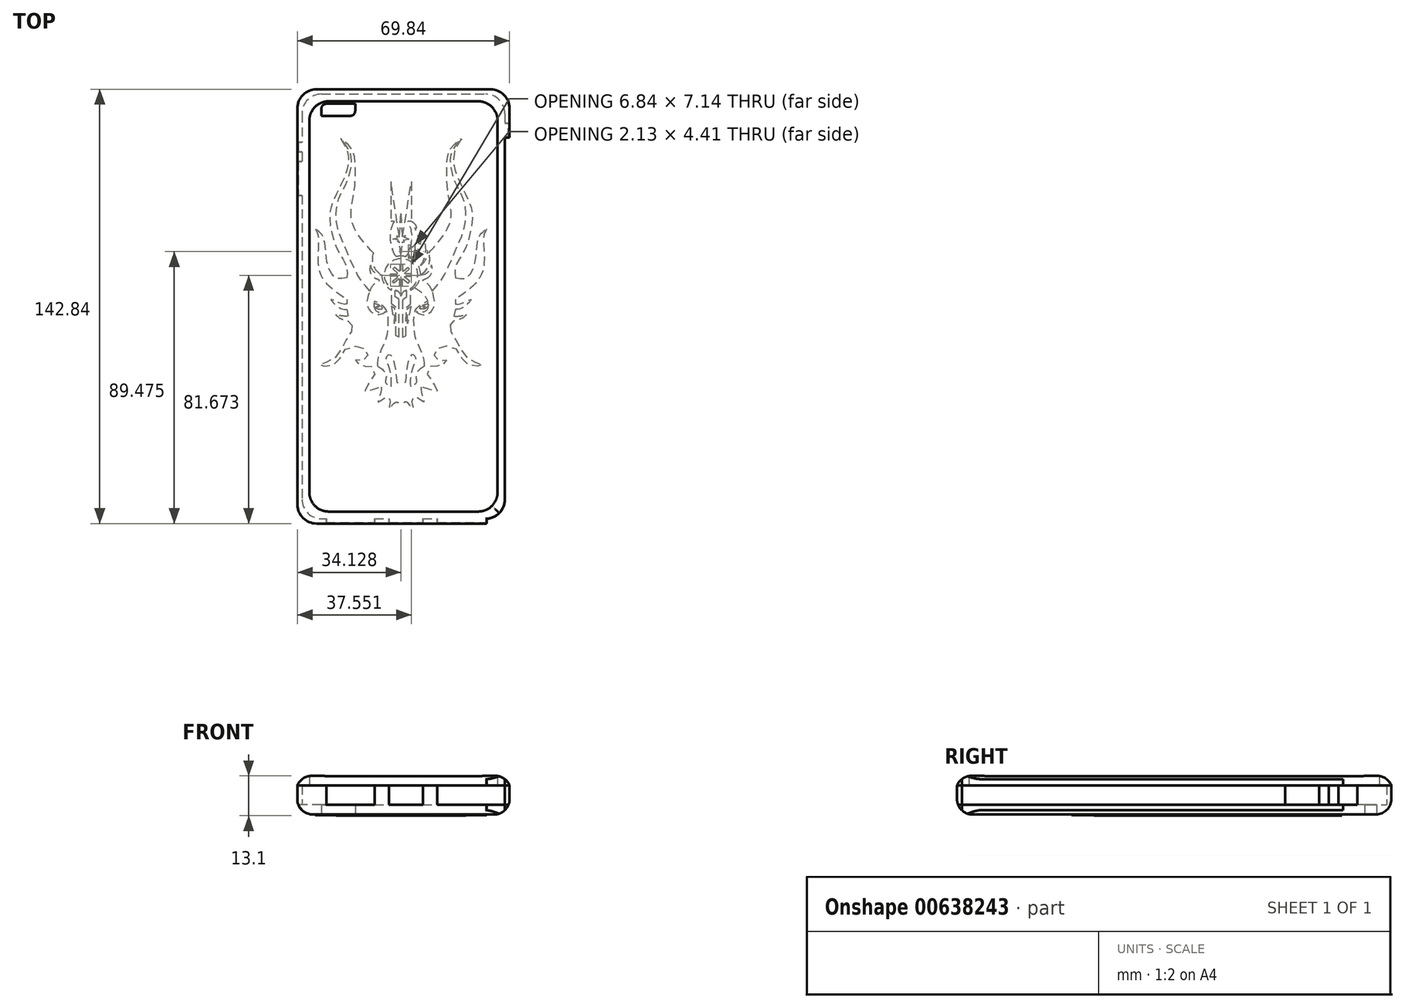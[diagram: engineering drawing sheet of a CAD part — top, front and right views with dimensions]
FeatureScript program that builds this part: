
annotation { "Feature Type Name" : "Feature", "Feature Type Description" : "" }
export const myFeature = defineFeature(function(context is Context, id is Id, definition is map)
    precondition{}
    {
        {
            var Q0;
            Q0=qCreatedBy(makeId("Top.planeOp"),FACE);
            var sketch = newSketch(context, id + "F0", { "sketchPlane" : qUnion([Q0])});
            skLineSegment(sketch, "E0.bottom", {"start": v(-25.4, 66.66) * mm, "end": v(-15.87, 66.66) * mm});
            skLineSegment(sketch, "E0.top", {"start": v(-26.98, 62.7) * mm, "end": v(-17.45, 62.7) * mm});
            skLineSegment(sketch, "E0.left", {"start": v(-26.98, 65.07) * mm, "end": v(-26.98, 62.7) * mm});
            skLineSegment(sketch, "E0.right", {"start": v(-15.87, 66.66) * mm, "end": v(-15.87, 64.28) * mm});
            skArc(sketch, "E1.filletArc", {"start": v(-25.4, 66.66) * mm, "mid": v(-26.51, 66.2) * mm, "end": v(-26.98, 65.07) * mm});
            skArc(sketch, "E2.filletArc", {"start": v(-17.45, 62.7) * mm, "mid": v(-16.33, 63.16) * mm, "end": v(-15.87, 64.28) * mm});
            skLineSegment(sketch, "E3.bottom", {"start": v(-34.92, 50.83) * mm, "end": v(-33.34, 50.83) * mm});
            skLineSegment(sketch, "E3.top", {"start": v(-34.92, 54) * mm, "end": v(-33.34, 54) * mm});
            skLineSegment(sketch, "E4.bottom", {"start": v(-34.92, 47.66) * mm, "end": v(-33.34, 47.66) * mm});
            skLineSegment(sketch, "E4.top", {"start": v(-34.92, 36.55) * mm, "end": v(-33.34, 36.55) * mm});
            skLineSegment(sketch, "E5.bottom", {"start": v(34.92, 60.29) * mm, "end": v(33.33, 60.29) * mm});
            skLineSegment(sketch, "E5.top", {"start": v(34.92, 55.52) * mm, "end": v(33.33, 55.52) * mm});
            skLineSegment(sketch, "E6.bottom", {"start": v(26.99, -69.85) * mm, "end": v(-26.99, -69.85) * mm});
            skLineSegment(sketch, "E6.top", {"start": v(26.99, 69.85) * mm, "end": v(-26.99, 69.85) * mm});
            skLineSegment(sketch, "E6.left", {"start": v(33.34, -63.5) * mm, "end": v(33.34, 63.5) * mm});
            skLineSegment(sketch, "E6.right", {"start": v(-33.34, -63.5) * mm, "end": v(-33.34, 63.5) * mm});
            skPoint(sketch, "E6.middle", {"position": v(0, 0) * mm});
            skLineSegment(sketch, "E7.bottom", {"start": v(28.57, 71.42) * mm, "end": v(-28.57, 71.42) * mm});
            skLineSegment(sketch, "E7.top", {"start": v(28.57, -71.42) * mm, "end": v(-28.57, -71.42) * mm});
            skLineSegment(sketch, "E7.left", {"start": v(34.92, 65.07) * mm, "end": v(34.92, -65.07) * mm});
            skLineSegment(sketch, "E7.right", {"start": v(-34.92, 65.07) * mm, "end": v(-34.92, -65.07) * mm});
            skLineSegment(sketch, "E8.bottom", {"start": v(24.6, -67.47) * mm, "end": v(-24.6, -67.47) * mm});
            skLineSegment(sketch, "E8.top", {"start": v(24.6, 67.47) * mm, "end": v(-24.6, 67.47) * mm});
            skLineSegment(sketch, "E8.left", {"start": v(30.96, -61.12) * mm, "end": v(30.96, 61.12) * mm});
            skLineSegment(sketch, "E8.right", {"start": v(-30.96, -61.12) * mm, "end": v(-30.96, 61.12) * mm});
            skPoint(sketch, "E9.visualSharp", {"position": v(-30.96, -67.47) * mm});
            skPoint(sketch, "E10.visualSharp", {"position": v(30.96, -67.47) * mm});
            skPoint(sketch, "E11.visualSharp", {"position": v(33.34, -69.85) * mm});
            skPoint(sketch, "E12.visualSharp", {"position": v(-33.34, -69.85) * mm});
            skPoint(sketch, "E13.visualSharp", {"position": v(-34.92, -71.42) * mm});
            skPoint(sketch, "E14.visualSharp", {"position": v(34.92, -71.42) * mm});
            skPoint(sketch, "E15.visualSharp", {"position": v(-34.92, 71.42) * mm});
            skPoint(sketch, "E16.visualSharp", {"position": v(-33.34, 69.85) * mm});
            skPoint(sketch, "E17.visualSharp", {"position": v(-30.96, 67.47) * mm});
            skPoint(sketch, "E18.visualSharp", {"position": v(30.96, 67.47) * mm});
            skPoint(sketch, "E19.visualSharp", {"position": v(33.34, 69.85) * mm});
            skPoint(sketch, "E20.visualSharp", {"position": v(34.92, 71.42) * mm});
            skLineSegment(sketch, "E21", {"start": v(-28.57, -71.42) * mm, "end": v(28.57, -71.42) * mm});
            skLineSegment(sketch, "E22.bottom", {"start": v(-25.4, -71.42) * mm, "end": v(-9.52, -71.42) * mm});
            skLineSegment(sketch, "E22.top", {"start": v(-25.4, -69.85) * mm, "end": v(-9.52, -69.85) * mm});
            skLineSegment(sketch, "E22.left", {"start": v(-25.4, -71.42) * mm, "end": v(-25.4, -69.85) * mm});
            skLineSegment(sketch, "E22.right", {"start": v(-9.52, -71.42) * mm, "end": v(-9.52, -69.85) * mm});
            skLineSegment(sketch, "E23.bottom", {"start": v(-4.76, -71.42) * mm, "end": v(6.36, -71.42) * mm});
            skLineSegment(sketch, "E23.top", {"start": v(-4.76, -69.85) * mm, "end": v(6.36, -69.85) * mm});
            skLineSegment(sketch, "E23.left", {"start": v(-4.76, -71.42) * mm, "end": v(-4.76, -69.85) * mm});
            skLineSegment(sketch, "E23.right", {"start": v(6.36, -71.42) * mm, "end": v(6.36, -69.85) * mm});
            skLineSegment(sketch, "E24", {"start": v(-28.57, -71.42) * mm, "end": v(12.42, -71.42) * mm});
            skLineSegment(sketch, "E25", {"start": v(-28.57, -71.42) * mm, "end": v(11.12, -71.42) * mm});
            skLineSegment(sketch, "E26.bottom", {"start": v(11.12, -71.42) * mm, "end": v(27.4, -71.42) * mm});
            skLineSegment(sketch, "E26.top", {"start": v(11.12, -69.85) * mm, "end": v(27.4, -69.85) * mm});
            skLineSegment(sketch, "E26.left", {"start": v(11.12, -71.42) * mm, "end": v(11.12, -69.85) * mm});
            skLineSegment(sketch, "E26.right", {"start": v(27.4, -71.42) * mm, "end": v(27.4, -69.85) * mm});
            skLineSegment(sketch, "E27", {"start": v(-24.6, -67.47) * mm, "end": v(24.6, -67.47) * mm});
            skLineSegment(sketch, "E28", {"start": v(-33.34, 63.5) * mm, "end": v(-33.34, -63.5) * mm});
            skLineSegment(sketch, "E29", {"start": v(-26.99, -69.85) * mm, "end": v(27.4, -69.85) * mm});
            skLineSegment(sketch, "E30", {"start": v(33.34, -69.85) * mm, "end": v(33.34, -69.27) * mm});
            skLineSegment(sketch, "E31", {"start": v(-28.57, 71.42) * mm, "end": v(28.57, 71.42) * mm});
            skLineSegment(sketch, "E32", {"start": v(34.92, -65.07) * mm, "end": v(34.92, 65.07) * mm});
            skLineSegment(sketch, "E33", {"start": v(-34.92, -65.07) * mm, "end": v(-34.92, 65.07) * mm});
            skArc(sketch, "E34.filletArc", {"start": v(-30.96, -61.12) * mm, "mid": v(-29.1, -65.6) * mm, "end": v(-24.6, -67.47) * mm});
            skArc(sketch, "E35.filletArc", {"start": v(-33.34, -63.5) * mm, "mid": v(-31.48, -68) * mm, "end": v(-26.99, -69.85) * mm});
            skArc(sketch, "E36.filletArc", {"start": v(-34.92, -65.07) * mm, "mid": v(-33.06, -69.56) * mm, "end": v(-28.57, -71.42) * mm});
            skArc(sketch, "E37.filletArc", {"start": v(28.57, -71.42) * mm, "mid": v(33.06, -69.56) * mm, "end": v(34.92, -65.07) * mm});
            skArc(sketch, "E38.filletArc", {"start": v(26.99, -69.85) * mm, "mid": v(31.48, -68) * mm, "end": v(33.34, -63.5) * mm});
            skArc(sketch, "E39.filletArc", {"start": v(24.6, -67.47) * mm, "mid": v(29.1, -65.6) * mm, "end": v(30.96, -61.12) * mm});
            skArc(sketch, "E40.filletArc", {"start": v(-24.6, 67.47) * mm, "mid": v(-29.1, 65.6) * mm, "end": v(-30.96, 61.12) * mm});
            skArc(sketch, "E41.filletArc", {"start": v(-26.99, 69.85) * mm, "mid": v(-31.48, 68) * mm, "end": v(-33.34, 63.5) * mm});
            skArc(sketch, "E42.filletArc", {"start": v(-28.57, 71.42) * mm, "mid": v(-33.06, 69.56) * mm, "end": v(-34.92, 65.07) * mm});
            skArc(sketch, "E43.filletArc", {"start": v(34.92, 65.07) * mm, "mid": v(33.06, 69.56) * mm, "end": v(28.57, 71.42) * mm});
            skArc(sketch, "E44.filletArc", {"start": v(33.34, 63.5) * mm, "mid": v(31.48, 68) * mm, "end": v(26.99, 69.85) * mm});
            skArc(sketch, "E45.filletArc", {"start": v(30.96, 61.12) * mm, "mid": v(29.1, 65.6) * mm, "end": v(24.6, 67.47) * mm});
            skLineSegment(sketch, "E46.trimOffspring", {"start": v(32.75, -69.85) * mm, "end": v(33.34, -69.85) * mm});
            skSolve(sketch);
        }
        {
            var Q0;
            Q0=makeQuery(id+"F0.imprint","IMPRINT",FACE,{"disambiguationData":[TD([[makeQuery(id+"F0.imprint","IMPRINT",EDGE,{"derivedFrom":sQuery(id+"F0.wireOp",EDGE,"E0.bottom")}),1.0]])]});
            var Q1;
            Q1=makeQuery(id+"F0.imprint","IMPRINT",FACE,{"disambiguationData":[TD([[makeQuery(id+"F0.imprint","IMPRINT",EDGE,{"derivedFrom":sQuery(id+"F0.wireOp",EDGE,"E8.right")}),1.0]])]});
            var Q2;
            {var subQ0=sQuery(id+"F0.wireOp",EDGE,"E28");var subQ1=sQuery(id+"F0.wireOp",EDGE,"E3.bottom");var subQ2=makeQuery(id+"F0.imprint","INTERSECT",VERTEX,{"derivedFrom":[subQ1,subQ0]});Q2=makeQuery(id+"F0.imprint","IMPRINT",FACE,{"disambiguationData":[TD([[makeQuery(id+"F0.imprint","IMPRINT",EDGE,{"disambiguationData":[TD([[subQ2,1.0]])],"derivedFrom":subQ1}),1.0]])]});}
            var Q3;
            {var subQ0=sQuery(id+"F0.wireOp",EDGE,"E28");var subQ1=sQuery(id+"F0.wireOp",EDGE,"E3.bottom");var subQ2=makeQuery(id+"F0.imprint","INTERSECT",VERTEX,{"derivedFrom":[subQ1,subQ0]});Q3=makeQuery(id+"F0.imprint","IMPRINT",FACE,{"disambiguationData":[TD([[makeQuery(id+"F0.imprint","IMPRINT",EDGE,{"disambiguationData":[TD([[subQ2,1.0]])],"derivedFrom":subQ1}),-1.0]])]});}
            var Q4;
            {var subQ0=sQuery(id+"F0.wireOp",EDGE,"E28");var subQ1=sQuery(id+"F0.wireOp",EDGE,"E4.bottom");var subQ2=makeQuery(id+"F0.imprint","INTERSECT",VERTEX,{"derivedFrom":[subQ1,subQ0]});Q4=makeQuery(id+"F0.imprint","IMPRINT",FACE,{"disambiguationData":[TD([[makeQuery(id+"F0.imprint","IMPRINT",EDGE,{"disambiguationData":[TD([[subQ2,1.0]])],"derivedFrom":subQ1}),-1.0]])]});}
            var Q5;
            Q5=makeQuery(id+"F0.imprint","IMPRINT",FACE,{"disambiguationData":[TD([[makeQuery(id+"F0.imprint","IMPRINT",EDGE,{"derivedFrom":sQuery(id+"F0.wireOp",EDGE,"E6.top")}),-1.0]])]});
            var Q6;
            {var subQ5=sQuery(id+"F0.wireOp",EDGE,"E22.left");Q6=makeQuery(id+"F0.imprint","IMPRINT",FACE,{"disambiguationData":[TD([[makeQuery(id+"F0.imprint","IMPRINT",EDGE,{"derivedFrom":subQ5}),1.0]])]});}
            var Q7;
            {var subQ0=sQuery(id+"F0.wireOp",EDGE,"E32");var subQ1=sQuery(id+"F0.wireOp",EDGE,"E5.bottom");var subQ2=makeQuery(id+"F0.imprint","INTERSECT",VERTEX,{"derivedFrom":[subQ1,subQ0]});Q7=makeQuery(id+"F0.imprint","IMPRINT",FACE,{"disambiguationData":[TD([[makeQuery(id+"F0.imprint","IMPRINT",EDGE,{"disambiguationData":[TD([[subQ2,-1.0]])],"derivedFrom":subQ1}),1.0]])]});}
            var Q8;
            {var subQ3=sQuery(id+"F0.wireOp",EDGE,"E21");Q8=makeQuery(id+"F0.imprint","IMPRINT",FACE,{"disambiguationData":[TD([[makeQuery(id+"F0.imprint","IMPRINT",EDGE,{"derivedFrom":subQ3}),1.0]])]});}
            var Q9;
            {var subQ2=sQuery(id+"F0.wireOp",EDGE,"E26.left");Q9=makeQuery(id+"F0.imprint","IMPRINT",FACE,{"disambiguationData":[TD([[makeQuery(id+"F0.imprint","IMPRINT",EDGE,{"derivedFrom":subQ2}),-1.0]])]});}
            var Q10;
            {var subQ0=sQuery(id+"F0.wireOp",EDGE,"E23.right");Q10=makeQuery(id+"F0.imprint","IMPRINT",FACE,{"disambiguationData":[TD([[makeQuery(id+"F0.imprint","IMPRINT",EDGE,{"derivedFrom":subQ0}),-1.0]])]});}
            var Q11;
            {var subQ0=sQuery(id+"F0.wireOp",EDGE,"E23.left");Q11=makeQuery(id+"F0.imprint","IMPRINT",FACE,{"disambiguationData":[TD([[makeQuery(id+"F0.imprint","IMPRINT",EDGE,{"derivedFrom":subQ0}),-1.0]])]});}
            var Q12;
            {var subQ0=sQuery(id+"F0.wireOp",EDGE,"E22.right");Q12=makeQuery(id+"F0.imprint","IMPRINT",FACE,{"disambiguationData":[TD([[makeQuery(id+"F0.imprint","IMPRINT",EDGE,{"derivedFrom":subQ0}),-1.0]])]});}
            var Q13;
            {var subQ0=sQuery(id+"F0.wireOp",EDGE,"E22.left");Q13=makeQuery(id+"F0.imprint","IMPRINT",FACE,{"disambiguationData":[TD([[makeQuery(id+"F0.imprint","IMPRINT",EDGE,{"derivedFrom":subQ0}),-1.0]])]});}
            extrude(context, id + "F1", {"entities" : qUnion([Q0, Q1, Q2, Q3, Q4, Q5, Q6, Q7, Q8, Q9, Q10, Q11, Q12, Q13]), "depth" : 3.17 * mm, "offsetDistance" : 25.4 * mm});
        }
        {
            var Q0;
            {var subQ5=sQuery(id+"F0.wireOp",EDGE,"E22.left");Q0=makeQuery(id+"F0.imprint","IMPRINT",FACE,{"disambiguationData":[TD([[makeQuery(id+"F0.imprint","IMPRINT",EDGE,{"derivedFrom":subQ5}),1.0]])]});}
            var Q1;
            {var subQ0=sQuery(id+"F0.wireOp",EDGE,"E28");var subQ1=sQuery(id+"F0.wireOp",EDGE,"E3.bottom");var subQ2=makeQuery(id+"F0.imprint","INTERSECT",VERTEX,{"derivedFrom":[subQ1,subQ0]});Q1=makeQuery(id+"F0.imprint","IMPRINT",FACE,{"disambiguationData":[TD([[makeQuery(id+"F0.imprint","IMPRINT",EDGE,{"disambiguationData":[TD([[subQ2,1.0]])],"derivedFrom":subQ1}),-1.0]])]});}
            var Q2;
            Q2=makeQuery(id+"F0.imprint","IMPRINT",FACE,{"disambiguationData":[TD([[makeQuery(id+"F0.imprint","IMPRINT",EDGE,{"derivedFrom":sQuery(id+"F0.wireOp",EDGE,"E6.top")}),-1.0]])]});
            var Q3;
            {var subQ3=sQuery(id+"F0.wireOp",EDGE,"E21");Q3=makeQuery(id+"F0.imprint","IMPRINT",FACE,{"disambiguationData":[TD([[makeQuery(id+"F0.imprint","IMPRINT",EDGE,{"derivedFrom":subQ3}),1.0]])]});}
            var Q4;
            {var subQ0=sQuery(id+"F0.wireOp",EDGE,"E22.right");Q4=makeQuery(id+"F0.imprint","IMPRINT",FACE,{"disambiguationData":[TD([[makeQuery(id+"F0.imprint","IMPRINT",EDGE,{"derivedFrom":subQ0}),-1.0]])]});}
            var Q5;
            {var subQ0=sQuery(id+"F0.wireOp",EDGE,"E23.right");Q5=makeQuery(id+"F0.imprint","IMPRINT",FACE,{"disambiguationData":[TD([[makeQuery(id+"F0.imprint","IMPRINT",EDGE,{"derivedFrom":subQ0}),-1.0]])]});}
            extrude(context, id + "F2", {"entities" : qUnion([Q0, Q1, Q2, Q3, Q4, Q5]), "operationType" : NewBodyOperationType.ADD, "depth" : 9.52 * mm, "offsetDistance" : 25.4 * mm});
        }
        {
            var Q0;
            Q0=makeQuery(id+"F0.imprint","IMPRINT",FACE,{"disambiguationData":[TD([[makeQuery(id+"F0.imprint","IMPRINT",EDGE,{"derivedFrom":sQuery(id+"F0.wireOp",EDGE,"E8.right")}),1.0]])]});
            var Q1;
            {var subQ0=sQuery(id+"F0.wireOp",EDGE,"E28");var subQ1=sQuery(id+"F0.wireOp",EDGE,"E4.bottom");var subQ2=makeQuery(id+"F0.imprint","INTERSECT",VERTEX,{"derivedFrom":[subQ1,subQ0]});Q1=makeQuery(id+"F0.imprint","IMPRINT",FACE,{"disambiguationData":[TD([[makeQuery(id+"F0.imprint","IMPRINT",EDGE,{"disambiguationData":[TD([[subQ2,1.0]])],"derivedFrom":subQ1}),-1.0]])]});}
            var Q2;
            {var subQ0=sQuery(id+"F0.wireOp",EDGE,"E28");var subQ1=sQuery(id+"F0.wireOp",EDGE,"E3.bottom");var subQ2=makeQuery(id+"F0.imprint","INTERSECT",VERTEX,{"derivedFrom":[subQ1,subQ0]});Q2=makeQuery(id+"F0.imprint","IMPRINT",FACE,{"disambiguationData":[TD([[makeQuery(id+"F0.imprint","IMPRINT",EDGE,{"disambiguationData":[TD([[subQ2,1.0]])],"derivedFrom":subQ1}),-1.0]])]});}
            var Q3;
            {var subQ0=sQuery(id+"F0.wireOp",EDGE,"E28");var subQ1=sQuery(id+"F0.wireOp",EDGE,"E3.bottom");var subQ2=makeQuery(id+"F0.imprint","INTERSECT",VERTEX,{"derivedFrom":[subQ1,subQ0]});Q3=makeQuery(id+"F0.imprint","IMPRINT",FACE,{"disambiguationData":[TD([[makeQuery(id+"F0.imprint","IMPRINT",EDGE,{"disambiguationData":[TD([[subQ2,1.0]])],"derivedFrom":subQ1}),1.0]])]});}
            var Q4;
            Q4=makeQuery(id+"F0.imprint","IMPRINT",FACE,{"disambiguationData":[TD([[makeQuery(id+"F0.imprint","IMPRINT",EDGE,{"derivedFrom":sQuery(id+"F0.wireOp",EDGE,"E6.top")}),-1.0]])]});
            var Q5;
            {var subQ5=sQuery(id+"F0.wireOp",EDGE,"E22.left");Q5=makeQuery(id+"F0.imprint","IMPRINT",FACE,{"disambiguationData":[TD([[makeQuery(id+"F0.imprint","IMPRINT",EDGE,{"derivedFrom":subQ5}),1.0]])]});}
            var Q6;
            {var subQ0=sQuery(id+"F0.wireOp",EDGE,"E32");var subQ1=sQuery(id+"F0.wireOp",EDGE,"E5.bottom");var subQ2=makeQuery(id+"F0.imprint","INTERSECT",VERTEX,{"derivedFrom":[subQ1,subQ0]});Q6=makeQuery(id+"F0.imprint","IMPRINT",FACE,{"disambiguationData":[TD([[makeQuery(id+"F0.imprint","IMPRINT",EDGE,{"disambiguationData":[TD([[subQ2,-1.0]])],"derivedFrom":subQ1}),1.0]])]});}
            var Q7;
            {var subQ3=sQuery(id+"F0.wireOp",EDGE,"E21");Q7=makeQuery(id+"F0.imprint","IMPRINT",FACE,{"disambiguationData":[TD([[makeQuery(id+"F0.imprint","IMPRINT",EDGE,{"derivedFrom":subQ3}),1.0]])]});}
            var Q8;
            {var subQ0=sQuery(id+"F0.wireOp",EDGE,"E22.left");Q8=makeQuery(id+"F0.imprint","IMPRINT",FACE,{"disambiguationData":[TD([[makeQuery(id+"F0.imprint","IMPRINT",EDGE,{"derivedFrom":subQ0}),-1.0]])]});}
            var Q9;
            {var subQ0=sQuery(id+"F0.wireOp",EDGE,"E22.right");Q9=makeQuery(id+"F0.imprint","IMPRINT",FACE,{"disambiguationData":[TD([[makeQuery(id+"F0.imprint","IMPRINT",EDGE,{"derivedFrom":subQ0}),-1.0]])]});}
            var Q10;
            {var subQ0=sQuery(id+"F0.wireOp",EDGE,"E23.left");Q10=makeQuery(id+"F0.imprint","IMPRINT",FACE,{"disambiguationData":[TD([[makeQuery(id+"F0.imprint","IMPRINT",EDGE,{"derivedFrom":subQ0}),-1.0]])]});}
            var Q11;
            {var subQ0=sQuery(id+"F0.wireOp",EDGE,"E23.right");Q11=makeQuery(id+"F0.imprint","IMPRINT",FACE,{"disambiguationData":[TD([[makeQuery(id+"F0.imprint","IMPRINT",EDGE,{"derivedFrom":subQ0}),-1.0]])]});}
            var Q12;
            {var subQ2=sQuery(id+"F0.wireOp",EDGE,"E26.left");Q12=makeQuery(id+"F0.imprint","IMPRINT",FACE,{"disambiguationData":[TD([[makeQuery(id+"F0.imprint","IMPRINT",EDGE,{"derivedFrom":subQ2}),-1.0]])]});}
            extrude(context, id + "F3", {"entities" : qUnion([Q0, Q1, Q2, Q3, Q4, Q5, Q6, Q7, Q8, Q9, Q10, Q11, Q12]), "depth" : 12.7 * mm, "offsetDistance" : 25.4 * mm, "hasSecondDirection" : true, "secondDirectionOppositeDirection" : false, "secondDirectionDepth" : 9.52 * mm});
        }
        {
            var Q0;
            Q0=makeQuery(id+"F3.opExtrude","CAP_EDGE",EDGE,{"disambiguationData":[OSD([sQuery(id+"F0.wireOp",EDGE,"E32")])],"isStart":false});
            var Q1;
            Q1=makeQuery(id+"F3.opExtrude","CAP_EDGE",EDGE,{"disambiguationData":[OSD([sQuery(id+"F0.wireOp",EDGE,"E37.filletArc")])],"isStart":false});
            var Q2;
            Q2=makeQuery(id+"F3.opExtrude","CAP_EDGE",EDGE,{"disambiguationData":[OSD([sQuery(id+"F0.wireOp",EDGE,"E21"),sQuery(id+"F0.wireOp",EDGE,"E25"),sQuery(id+"F0.wireOp",EDGE,"E26.bottom")])],"isStart":false});
            var Q3;
            Q3=makeQuery(id+"F3.opExtrude","CAP_EDGE",EDGE,{"disambiguationData":[OSD([sQuery(id+"F0.wireOp",EDGE,"E36.filletArc")])],"isStart":false});
            var Q4;
            Q4=makeQuery(id+"F3.opExtrude","CAP_EDGE",EDGE,{"disambiguationData":[OSD([sQuery(id+"F0.wireOp",EDGE,"E33")])],"isStart":false});
            var Q5;
            Q5=makeQuery(id+"F3.opExtrude","CAP_EDGE",EDGE,{"disambiguationData":[OSD([sQuery(id+"F0.wireOp",EDGE,"E42.filletArc")])],"isStart":false});
            var Q6;
            Q6=makeQuery(id+"F3.opExtrude","CAP_EDGE",EDGE,{"disambiguationData":[OSD([sQuery(id+"F0.wireOp",EDGE,"E31")])],"isStart":false});
            var Q7;
            Q7=makeQuery(id+"F3.opExtrude","CAP_EDGE",EDGE,{"disambiguationData":[OSD([sQuery(id+"F0.wireOp",EDGE,"E43.filletArc")])],"isStart":false});
            fillet(context, id + "F4", {"entities" : qUnion([Q0, Q1, Q2, Q3, Q4, Q5, Q6, Q7]), "radius" : 5.08 * mm, "tangentPropagation" : true, "allowEdgeOverflow" : false});
        }
        {
            var Q0;
            Q0=makeQuery(id+"F1.opExtrude","CAP_EDGE",EDGE,{"disambiguationData":[OSD([sQuery(id+"F0.wireOp",EDGE,"E33")])],"isStart":true});
            var Q1;
            Q1=makeQuery(id+"F1.opExtrude","CAP_EDGE",EDGE,{"disambiguationData":[OSD([sQuery(id+"F0.wireOp",EDGE,"E42.filletArc")])],"isStart":true});
            var Q2;
            Q2=makeQuery(id+"F1.opExtrude","CAP_EDGE",EDGE,{"disambiguationData":[OSD([sQuery(id+"F0.wireOp",EDGE,"E31")])],"isStart":true});
            var Q3;
            Q3=makeQuery(id+"F1.opExtrude","CAP_EDGE",EDGE,{"disambiguationData":[OSD([sQuery(id+"F0.wireOp",EDGE,"E43.filletArc")])],"isStart":true});
            var Q4;
            Q4=makeQuery(id+"F1.opExtrude","CAP_EDGE",EDGE,{"disambiguationData":[OSD([sQuery(id+"F0.wireOp",EDGE,"E32")])],"isStart":true});
            var Q5;
            Q5=makeQuery(id+"F1.opExtrude","CAP_EDGE",EDGE,{"disambiguationData":[OSD([sQuery(id+"F0.wireOp",EDGE,"E36.filletArc")])],"isStart":true});
            var Q6;
            Q6=makeQuery(id+"F1.opExtrude","CAP_EDGE",EDGE,{"disambiguationData":[OSD([sQuery(id+"F0.wireOp",EDGE,"E21"),sQuery(id+"F0.wireOp",EDGE,"E25"),sQuery(id+"F0.wireOp",EDGE,"E26.bottom")])],"isStart":true});
            var Q7;
            Q7=makeQuery(id+"F1.opExtrude","CAP_EDGE",EDGE,{"disambiguationData":[OSD([sQuery(id+"F0.wireOp",EDGE,"E37.filletArc")])],"isStart":true});
            fillet(context, id + "F5", {"entities" : qUnion([Q0, Q1, Q2, Q3, Q4, Q5, Q6, Q7]), "radius" : 5.08 * mm, "tangentPropagation" : true, "allowEdgeOverflow" : false});
        }
        {
            var Q0;
            Q0=qCreatedBy(makeId("Top.planeOp"),FACE);
            var sketch = newSketch(context, id + "F6", { "sketchPlane" : qUnion([Q0])});
            skLineSegment(sketch, "E47", {"start": v(-0.16, -10.06) * mm, "end": v(0.84, -9.56) * mm});
            skLineSegment(sketch, "E48", {"start": v(0.84, -9.56) * mm, "end": v(0.93, -0.32) * mm});
            skLineSegment(sketch, "E49", {"start": v(0.93, -0.32) * mm, "end": v(2.34, 0.78) * mm});
            skLineSegment(sketch, "E50", {"start": v(-0.16, -10.06) * mm, "end": v(-0.16, 2.37) * mm});
            skLineSegment(sketch, "E51", {"start": v(-0.16, 2.37) * mm, "end": v(1.12, 3.23) * mm});
            skLineSegment(sketch, "E52", {"start": v(1.12, 3.23) * mm, "end": v(1.12, 5.28) * mm});
            skArc(sketch, "E53", {"start": v(-0.8, 5) * mm, "mid": v(4.73, 10.33) * mm, "end": v(-0.8, 15.67) * mm});
            skLineSegment(sketch, "E54", {"start": v(2.34, 0.78) * mm, "end": v(2.3, 5.84) * mm});
            skLineSegment(sketch, "E55", {"start": v(2, 18.88) * mm, "end": v(3.7, 20.26) * mm});
            skLineSegment(sketch, "E56", {"start": v(3.7, 20.26) * mm, "end": v(3.7, 17.07) * mm});
            skLineSegment(sketch, "E57", {"start": v(3.7, 17.07) * mm, "end": v(2.47, 15.85) * mm});
            skLineSegment(sketch, "E58", {"start": v(2.47, 15.85) * mm, "end": v(1.57, 17.44) * mm});
            skArc(sketch, "E59", {"start": v(2, 18.88) * mm, "mid": v(2.8, 23.51) * mm, "end": v(1.46, 28.02) * mm});
            skArc(sketch, "E60", {"start": v(0.61, 16.38) * mm, "mid": v(1.15, 16.85) * mm, "end": v(1.57, 17.44) * mm});
            skArc(sketch, "E61", {"start": v(4.4, 25.8) * mm, "mid": v(3.37, 27.5) * mm, "end": v(1.46, 28.02) * mm});
            skArc(sketch, "E62", {"start": v(3.87, 16.13) * mm, "mid": v(5.16, 21) * mm, "end": v(3.7, 25.8) * mm});
            skArc(sketch, "E63", {"start": v(3.87, 16.13) * mm, "mid": v(5.61, 20.27) * mm, "end": v(5.62, 24.76) * mm});
            skArc(sketch, "E64", {"start": v(7.08, 22.96) * mm, "mid": v(6.62, 24.08) * mm, "end": v(5.62, 24.76) * mm});
            skArc(sketch, "E65", {"start": v(5.62, 13.44) * mm, "mid": v(7.36, 18.1) * mm, "end": v(6.23, 22.96) * mm});
            skArc(sketch, "E66", {"start": v(5.62, 13.44) * mm, "mid": v(7.45, 15.64) * mm, "end": v(7.93, 18.47) * mm});
            skArc(sketch, "E67", {"start": v(5.62, 10.4) * mm, "mid": v(8.43, 13.96) * mm, "end": v(7.93, 18.47) * mm});
            skArc(sketch, "E68", {"start": v(5.62, 10.4) * mm, "mid": v(8.03, 11.29) * mm, "end": v(9.21, 13.57) * mm});
            skArc(sketch, "E69", {"start": v(7.08, 9) * mm, "mid": v(9.17, 10.81) * mm, "end": v(9.21, 13.57) * mm});
            skArc(sketch, "E70", {"start": v(3.6, 6.23) * mm, "mid": v(5.38, 12.27) * mm, "end": v(0.61, 16.38) * mm});
            skLineSegment(sketch, "E71", {"start": v(1.32, -0.78) * mm, "end": v(2.45, 0.08) * mm});
            skLineSegment(sketch, "E72", {"start": v(2.45, 0.08) * mm, "end": v(1.34, -5.67) * mm});
            skLineSegment(sketch, "E73", {"start": v(1.34, -5.67) * mm, "end": v(1.32, -0.78) * mm});
            skFitSpline(sketch, "E74", {"points": [v(3.6, 6.23) * mm, v(6.58, 4) * mm, v(7.91, 1.72) * mm, v(8, -0.37) * mm, v(7, -1.73) * mm, v(5.03, -1.92) * mm, v(4.12, -1.7) * mm], "startDerivative": vector(14.8, -9.52) * mm, "endDerivative": vector(-7.08, 2.25) * mm});
            skFitSpline(sketch, "E75", {"points": [v(4.12, -1.7) * mm, v(5.5, -2.52) * mm, v(8.07, -2.49) * mm, v(10.12, 0.14) * mm, v(10.06, 2.7) * mm, v(8.16, 7.25) * mm, v(6.36, 8.55) * mm, v(7.08, 9) * mm], "startDerivative": vector(10.53, -7.87) * mm, "endDerivative": vector(13.03, 5.28) * mm});
            skLineSegment(sketch, "E76", {"start": v(-0.8, 16.9) * mm, "end": v(-0.27, 20.83) * mm});
            skLineSegment(sketch, "E77", {"start": v(-0.27, 20.83) * mm, "end": v(-0.27, 21.3) * mm});
            skLineSegment(sketch, "E78", {"start": v(-0.27, 21.3) * mm, "end": v(0.32, 21.3) * mm});
            skLineSegment(sketch, "E79", {"start": v(0.32, 21.3) * mm, "end": v(0.1, 21.91) * mm});
            skLineSegment(sketch, "E80", {"start": v(0.1, 21.91) * mm, "end": v(1.85, 22.15) * mm});
            skLineSegment(sketch, "E81", {"start": v(1.85, 22.15) * mm, "end": v(0.26, 22.62) * mm});
            skLineSegment(sketch, "E82", {"start": v(0.26, 22.62) * mm, "end": v(0.64, 23.3) * mm});
            skLineSegment(sketch, "E83", {"start": v(0.64, 23.3) * mm, "end": v(-0.25, 22.92) * mm});
            skLineSegment(sketch, "E84", {"start": v(3.7, 25.8) * mm, "end": v(4.4, 25.8) * mm});
            skLineSegment(sketch, "E85", {"start": v(6.23, 22.96) * mm, "end": v(7.08, 22.96) * mm});
            skLineSegment(sketch, "E86", {"start": v(-0.25, 22.92) * mm, "end": v(-0.8, 31.03) * mm});
            skFitSpline(sketch, "E87", {"points": [v(8.31, 17.62) * mm, v(10.78, 20.35) * mm, v(15.43, 28.02) * mm, v(14.71, 37.16) * mm, v(14.25, 45.86) * mm, v(15.26, 51.42) * mm, v(19.05, 55.21) * mm], "startDerivative": vector(17.57, 18.84) * mm, "endDerivative": vector(30.07, 23.23) * mm});
            skFitSpline(sketch, "E88", {"points": [v(19.05, 55.21) * mm, v(17.15, 51.8) * mm, v(16.78, 45.6) * mm, v(21.7, 34.22) * mm, v(22.6, 28.02) * mm, v(20.06, 18.47) * mm, v(17.15, 13.26) * mm, v(17.03, 9.47) * mm], "startDerivative": vector(-19, -28.92) * mm, "endDerivative": vector(3.8, -35.47) * mm});
            skFitSpline(sketch, "E89", {"points": [v(17.03, 9.47) * mm, v(20.7, 9.47) * mm, v(23.6, 14.9) * mm, v(24.87, 22.96) * mm, v(27.4, 25.4) * mm], "startDerivative": vector(18.53, -4.1) * mm, "endDerivative": vector(14.4, 8.9) * mm});
            skFitSpline(sketch, "E90", {"points": [v(27.4, 25.4) * mm, v(26.41, 22.96) * mm, v(26.41, 13.26) * mm, v(23.1, 6.94) * mm, v(17.03, 2.39) * mm], "startDerivative": vector(-7.89, -11.91) * mm, "endDerivative": vector(-24.05, -15.72) * mm});
            skFitSpline(sketch, "E91", {"points": [v(17.03, 0.8) * mm, v(19.05, 0.96) * mm, v(22.18, 2.29) * mm, v(21.4, 1.14) * mm, v(19.05, -0.64) * mm, v(17.03, -0.99) * mm], "startDerivative": vector(9, -1.2) * mm, "endDerivative": vector(-10.69, -0.53) * mm});
            skFitSpline(sketch, "E92", {"points": [v(16.62, -3.2) * mm, v(18.64, -3.14) * mm, v(20.72, -2.58) * mm], "startDerivative": vector(4.1, -0.14) * mm, "endDerivative": vector(4.08, 1.35) * mm});
            skFitSpline(sketch, "E93", {"points": [v(20.72, -2.58) * mm, v(19.68, -3.67) * mm, v(16.62, -4.79) * mm], "startDerivative": vector(-2.04, -2.86) * mm, "endDerivative": vector(-5.9, -1.63) * mm});
            skFitSpline(sketch, "E94", {"points": [v(15.43, -6.23) * mm, v(15.43, -7.8) * mm, v(18.02, -12.4) * mm, v(20.72, -16.75) * mm, v(24.87, -18.78) * mm, v(26.1, -19.3) * mm, v(23.32, -19.58) * mm, v(19.93, -18.1) * mm, v(17.03, -13.7) * mm, v(11.68, -13.67) * mm, v(10.12, -15.63) * mm, v(11.17, -17.65) * mm, v(14.2, -17.65) * mm, v(13.45, -18.66) * mm, v(11.62, -19.64) * mm, v(9.09, -19.58) * mm, v(7.93, -22.53) * mm, v(11.32, -27.54) * mm, v(9.27, -27.54) * mm, v(5.78, -26.46) * mm], "startDerivative": vector(-7.73, -38) * mm, "endDerivative": vector(-58.93, 20.62) * mm});
            skFitSpline(sketch, "E95", {"points": [v(5.78, -26.46) * mm, v(5.97, -28.68) * mm, v(6.72, -31.39) * mm, v(5.12, -30.43) * mm, v(3.47, -29.98) * mm, v(2.78, -31.12) * mm, v(3.02, -32.48) * mm, v(3, -33.58) * mm, v(2.52, -33.56) * mm, v(2.14, -32.47) * mm, v(1.1, -31.57) * mm, v(0.32, -31.46) * mm, v(0.02, -32.29) * mm, v(-0.8, -32.72) * mm], "startDerivative": vector(-1, -19.1) * mm, "endDerivative": vector(-15.31, -4.03) * mm});
            skFitSpline(sketch, "E96", {"points": [v(5.78, -26.46) * mm, v(5.78, -22.53) * mm, v(6.89, -19.62) * mm, v(5.78, -14.52) * mm, v(4.16, -10.91) * mm, v(3.47, -6.36) * mm, v(4.12, -0.98) * mm, v(7.91, 1.72) * mm], "startDerivative": vector(-3.54, 31.13) * mm, "endDerivative": vector(30.9, 14.24) * mm});
            skFitSpline(sketch, "E97", {"points": [v(9.44, 5.04) * mm, v(13.17, 9.8) * mm, v(17.15, 18.47) * mm, v(20.06, 26) * mm, v(20.06, 34.22) * mm, v(17.15, 40.66) * mm, v(15.6, 46.3) * mm, v(15.95, 50.59) * mm, v(19.05, 55.21) * mm], "startDerivative": vector(32.67, 35.42) * mm, "endDerivative": vector(33.02, 40.5) * mm});
            skFitSpline(sketch, "E98", {"points": [v(6.89, -19.62) * mm, v(4.12, -22.53) * mm, v(4.12, -25.34) * mm, v(0.02, -26.85) * mm, v(-0.8, -26.85) * mm], "startDerivative": vector(-12.98, -8.92) * mm, "endDerivative": vector(-4.07, 0.48) * mm});
            skFitSpline(sketch, "E99", {"points": [v(2.45, -26.34) * mm, v(2.45, -23.16) * mm, v(3.47, -19.2) * mm, v(4.12, -17.43) * mm, v(3.47, -15.96) * mm, v(2.45, -16.14) * mm, v(1.46, -18.55) * mm, v(0.84, -22.53) * mm, v(0.32, -25.48) * mm, v(-0.8, -25.93) * mm], "startDerivative": vector(-1.6, 23.43) * mm, "endDerivative": vector(-16.16, -2.15) * mm});
            skFitSpline(sketch, "E100", {"points": [v(5.37, -0.68) * mm, v(6.16, 0.25) * mm, v(8.1, 0.7) * mm, v(7.4, -0.56) * mm, v(5.37, -0.68) * mm]});
            skFitSpline(sketch, "E101", {"points": [v(6.16, 0.25) * mm, v(7.4, -0.56) * mm, v(7.14, -0.05) * mm, v(6.16, 0.25) * mm]});
            skLineSegment(sketch, "E102", {"start": v(-0.25, 22.92) * mm, "end": v(2.55, 41.02) * mm});
            skLineSegment(sketch, "E103", {"start": v(2.55, 41.02) * mm, "end": v(2.55, 27.92) * mm});
            skLineSegment(sketch, "E104", {"start": v(4.4, 25.8) * mm, "end": v(5.14, 30.38) * mm});
            skLineSegment(sketch, "E105", {"start": v(5.14, 30.38) * mm, "end": v(5.62, 24.76) * mm});
            skLineSegment(sketch, "E106", {"start": v(7.93, 18.47) * mm, "end": v(7.93, 22.52) * mm});
            skArc(sketch, "E107", {"start": v(-0.36, 8.98) * mm, "mid": v(-0.25, 9.02) * mm, "end": v(-0.14, 9.07) * mm});
            skLineSegment(sketch, "E108", {"start": v(-0.8, 13.82) * mm, "end": v(-0.34, 13.82) * mm});
            skLineSegment(sketch, "E109", {"start": v(-0.34, 13.82) * mm, "end": v(-0.34, 11.65) * mm});
            skLineSegment(sketch, "E110", {"start": v(-0.1, 11.54) * mm, "end": v(1.46, 12.92) * mm});
            skLineSegment(sketch, "E111", {"start": v(1.46, 12.92) * mm, "end": v(1.95, 12.37) * mm});
            skLineSegment(sketch, "E112", {"start": v(1.95, 12.37) * mm, "end": v(0.42, 11.02) * mm});
            skLineSegment(sketch, "E113", {"start": v(-0.8, 6.68) * mm, "end": v(-0.36, 6.68) * mm});
            skLineSegment(sketch, "E114", {"start": v(-0.36, 6.68) * mm, "end": v(-0.36, 8.98) * mm});
            skLineSegment(sketch, "E115", {"start": v(-0.14, 9.07) * mm, "end": v(1.58, 7.67) * mm});
            skLineSegment(sketch, "E116", {"start": v(1.58, 7.67) * mm, "end": v(2.07, 8.26) * mm});
            skLineSegment(sketch, "E117", {"start": v(2.07, 8.26) * mm, "end": v(0.42, 9.6) * mm});
            skLineSegment(sketch, "E118", {"start": v(0.54, 9.89) * mm, "end": v(2.63, 9.89) * mm});
            skLineSegment(sketch, "E119", {"start": v(2.63, 9.89) * mm, "end": v(2.63, 10.65) * mm});
            skLineSegment(sketch, "E120", {"start": v(2.63, 10.65) * mm, "end": v(0.56, 10.65) * mm});
            skArc(sketch, "E121.trimOffspring", {"start": v(0.56, 10.65) * mm, "mid": v(0.5, 10.84) * mm, "end": v(0.42, 11.02) * mm});
            skArc(sketch, "E122.trimOffspring", {"start": v(-0.1, 11.54) * mm, "mid": v(-0.22, 11.6) * mm, "end": v(-0.34, 11.65) * mm});
            skArc(sketch, "E123.trimOffspring", {"start": v(0.42, 9.6) * mm, "mid": v(0.49, 9.75) * mm, "end": v(0.54, 9.89) * mm});
            skPoint(sketch, "E124.orphan", {"position": v(-0.8, 8.9) * mm});
            skPoint(sketch, "E125.orphan", {"position": v(-0.8, 11.72) * mm});
            skLineSegment(sketch, "E126", {"start": v(15.43, -6.23) * mm, "end": v(16.62, -4.79) * mm});
            skLineSegment(sketch, "E127", {"start": v(17.03, -0.99) * mm, "end": v(16.62, -3.2) * mm});
            skLineSegment(sketch, "E128", {"start": v(17.03, 2.39) * mm, "end": v(17.03, 0.8) * mm});
            skArc(sketch, "E129.MirrorCS", {"start": v(-1.48, 11.54) * mm, "mid": v(-1.36, 11.6) * mm, "end": v(-1.24, 11.65) * mm});
            skLineSegment(sketch, "E130.MirrorCS", {"start": v(-2.12, 9.89) * mm, "end": v(-4.21, 9.89) * mm});
            skArc(sketch, "E131.MirrorCS", {"start": v(-2.15, 10.65) * mm, "mid": v(-2.09, 10.84) * mm, "end": v(-2, 11.02) * mm});
            skLineSegment(sketch, "E132.MirrorCS", {"start": v(-1.48, 11.54) * mm, "end": v(-3.05, 12.92) * mm});
            skLineSegment(sketch, "E133.MirrorCS", {"start": v(-0.8, 6.68) * mm, "end": v(-1.23, 6.68) * mm});
            skLineSegment(sketch, "E134.MirrorCS", {"start": v(-0.8, 13.82) * mm, "end": v(-1.24, 13.82) * mm});
            skLineSegment(sketch, "E135.MirrorCS", {"start": v(-3.17, 7.67) * mm, "end": v(-3.65, 8.26) * mm});
            skLineSegment(sketch, "E136.MirrorCS", {"start": v(-1.45, 9.07) * mm, "end": v(-3.17, 7.67) * mm});
            skLineSegment(sketch, "E137.MirrorCS", {"start": v(-4.21, 9.89) * mm, "end": v(-4.21, 10.65) * mm});
            skLineSegment(sketch, "E138.MirrorCS", {"start": v(-3.53, 12.37) * mm, "end": v(-2, 11.02) * mm});
            skLineSegment(sketch, "E139.MirrorCS", {"start": v(-3.05, 12.92) * mm, "end": v(-3.53, 12.37) * mm});
            skArc(sketch, "E140.MirrorCS", {"start": v(-2, 9.6) * mm, "mid": v(-2.07, 9.75) * mm, "end": v(-2.12, 9.89) * mm});
            skLineSegment(sketch, "E141.MirrorCS", {"start": v(-4.21, 10.65) * mm, "end": v(-2.15, 10.65) * mm});
            skLineSegment(sketch, "E142.MirrorCS", {"start": v(-3.65, 8.26) * mm, "end": v(-2, 9.6) * mm});
            skLineSegment(sketch, "E143.MirrorCS", {"start": v(-1.24, 13.82) * mm, "end": v(-1.24, 11.65) * mm});
            skLineSegment(sketch, "E144.MirrorCS", {"start": v(-1.23, 6.68) * mm, "end": v(-1.23, 8.98) * mm});
            skArc(sketch, "E145.MirrorCS", {"start": v(-1.23, 8.98) * mm, "mid": v(-1.34, 9.02) * mm, "end": v(-1.45, 9.07) * mm});
            skLineSegment(sketch, "E146.MirrorCS", {"start": v(-1.9, 21.3) * mm, "end": v(-1.68, 21.91) * mm});
            skLineSegment(sketch, "E147.MirrorCS", {"start": v(-1.32, 21.3) * mm, "end": v(-1.9, 21.3) * mm});
            skArc(sketch, "E148.MirrorCS", {"start": v(-2.2, 16.38) * mm, "mid": v(-2.74, 16.85) * mm, "end": v(-3.15, 17.44) * mm});
            skLineSegment(sketch, "E149.MirrorCS", {"start": v(-1.68, 21.91) * mm, "end": v(-3.44, 22.15) * mm});
            skLineSegment(sketch, "E150.MirrorCS", {"start": v(-0.8, 16.9) * mm, "end": v(-1.32, 20.83) * mm});
            skLineSegment(sketch, "E151.MirrorCS", {"start": v(-4.06, 15.85) * mm, "end": v(-3.15, 17.44) * mm});
            skLineSegment(sketch, "E152.MirrorCS", {"start": v(-5.28, 17.07) * mm, "end": v(-4.06, 15.85) * mm});
            skLineSegment(sketch, "E153.MirrorCS", {"start": v(-1.84, 22.62) * mm, "end": v(-2.22, 23.3) * mm});
            skLineSegment(sketch, "E154.MirrorCS", {"start": v(-5.28, 25.8) * mm, "end": v(-6, 25.8) * mm});
            skLineSegment(sketch, "E155.MirrorCS", {"start": v(-7.81, 22.96) * mm, "end": v(-8.66, 22.96) * mm});
            skLineSegment(sketch, "E156.MirrorCS", {"start": v(-1.32, 20.83) * mm, "end": v(-1.32, 21.3) * mm});
            skArc(sketch, "E157.MirrorCS", {"start": v(-0.8, 5) * mm, "mid": v(-6.32, 10.33) * mm, "end": v(-0.8, 15.67) * mm});
            skLineSegment(sketch, "E158.MirrorCS", {"start": v(-3.58, 18.88) * mm, "end": v(-5.28, 20.26) * mm});
            skLineSegment(sketch, "E159.MirrorCS", {"start": v(-5.28, 20.26) * mm, "end": v(-5.28, 17.07) * mm});
            skLineSegment(sketch, "E160.MirrorCS", {"start": v(-3.44, 22.15) * mm, "end": v(-1.84, 22.62) * mm});
            skArc(sketch, "E161.MirrorCS", {"start": v(-8.66, 22.96) * mm, "mid": v(-8.2, 24.08) * mm, "end": v(-7.2, 24.76) * mm});
            skArc(sketch, "E162.MirrorCS", {"start": v(-5.45, 16.13) * mm, "mid": v(-7.2, 20.27) * mm, "end": v(-7.2, 24.76) * mm});
            skArc(sketch, "E163.MirrorCS", {"start": v(-7.2, 13.44) * mm, "mid": v(-9.03, 15.64) * mm, "end": v(-9.51, 18.47) * mm});
            skArc(sketch, "E164.MirrorCS", {"start": v(-5.19, 6.23) * mm, "mid": v(-6.97, 12.27) * mm, "end": v(-2.2, 16.38) * mm});
            skFitSpline(sketch, "E165.MirrorCS", {"points": [v(-18.2, -3.2) * mm, v(-20.23, -3.14) * mm, v(-22.3, -2.58) * mm], "startDerivative": vector(-4.1, -0.14) * mm, "endDerivative": vector(-4.08, 1.35) * mm});
            skArc(sketch, "E166.MirrorCS", {"start": v(-5.45, 16.13) * mm, "mid": v(-6.74, 21) * mm, "end": v(-5.28, 25.8) * mm});
            skLineSegment(sketch, "E167.MirrorCS", {"start": v(-2.22, 23.3) * mm, "end": v(-1.33, 22.92) * mm});
            skLineSegment(sketch, "E168.MirrorCS", {"start": v(-2.9, -0.78) * mm, "end": v(-4.03, 0.08) * mm});
            skFitSpline(sketch, "E169.MirrorCS", {"points": [v(-5.19, 6.23) * mm, v(-8.17, 4) * mm, v(-9.5, 1.72) * mm, v(-9.59, -0.37) * mm, v(-8.58, -1.73) * mm, v(-6.62, -1.92) * mm, v(-5.7, -1.7) * mm], "startDerivative": vector(-14.8, -9.52) * mm, "endDerivative": vector(7.08, 2.25) * mm});
            skLineSegment(sketch, "E170.MirrorCS", {"start": v(-18.61, 2.39) * mm, "end": v(-18.61, 0.8) * mm});
            skLineSegment(sketch, "E171.MirrorCS", {"start": v(-2.92, -5.67) * mm, "end": v(-2.9, -0.78) * mm});
            skLineSegment(sketch, "E172.MirrorCS", {"start": v(-6, 25.8) * mm, "end": v(-6.72, 30.38) * mm});
            skLineSegment(sketch, "E173.MirrorCS", {"start": v(-9.51, 18.47) * mm, "end": v(-9.51, 22.52) * mm});
            skFitSpline(sketch, "E174.MirrorCS", {"points": [v(-5.7, -1.7) * mm, v(-7.1, -2.52) * mm, v(-9.65, -2.49) * mm, v(-11.7, 0.14) * mm, v(-11.64, 2.7) * mm, v(-9.75, 7.25) * mm, v(-7.95, 8.55) * mm, v(-8.66, 9) * mm], "startDerivative": vector(-10.53, -7.87) * mm, "endDerivative": vector(-13.03, 5.28) * mm});
            skArc(sketch, "E175.MirrorCS", {"start": v(-8.66, 9) * mm, "mid": v(-10.75, 10.81) * mm, "end": v(-10.8, 13.57) * mm});
            skArc(sketch, "E176.MirrorCS", {"start": v(-7.2, 13.44) * mm, "mid": v(-8.94, 18.1) * mm, "end": v(-7.81, 22.96) * mm});
            skFitSpline(sketch, "E177.MirrorC", {"points": [v(-6.96, -0.68) * mm, v(-7.75, 0.25) * mm, v(-9.68, 0.7) * mm, v(-8.99, -0.56) * mm, v(-6.96, -0.68) * mm]});
            skFitSpline(sketch, "E178.MirrorC", {"points": [v(-7.75, 0.25) * mm, v(-8.99, -0.56) * mm, v(-8.73, -0.05) * mm, v(-7.75, 0.25) * mm]});
            skArc(sketch, "E179.MirrorCS", {"start": v(-7.2, 10.4) * mm, "mid": v(-10.01, 13.96) * mm, "end": v(-9.51, 18.47) * mm});
            skLineSegment(sketch, "E180.MirrorCS", {"start": v(-18.61, -0.99) * mm, "end": v(-18.2, -3.2) * mm});
            skFitSpline(sketch, "E181.MirrorCS", {"points": [v(-22.3, -2.58) * mm, v(-21.26, -3.67) * mm, v(-18.2, -4.79) * mm], "startDerivative": vector(2.04, -2.86) * mm, "endDerivative": vector(5.9, -1.63) * mm});
            skLineSegment(sketch, "E182.MirrorCS", {"start": v(-1.43, -10.06) * mm, "end": v(-2.42, -9.56) * mm});
            skLineSegment(sketch, "E183.MirrorCS", {"start": v(-2.52, -0.32) * mm, "end": v(-3.93, 0.78) * mm});
            skLineSegment(sketch, "E184.MirrorCS", {"start": v(-1.43, 2.37) * mm, "end": v(-2.7, 3.23) * mm});
            skArc(sketch, "E185.MirrorCS", {"start": v(-7.2, 10.4) * mm, "mid": v(-9.62, 11.29) * mm, "end": v(-10.8, 13.57) * mm});
            skLineSegment(sketch, "E186.MirrorCS", {"start": v(-2.7, 3.23) * mm, "end": v(-2.7, 5.28) * mm});
            skLineSegment(sketch, "E187.MirrorCS", {"start": v(-4.03, 0.08) * mm, "end": v(-2.92, -5.67) * mm});
            skLineSegment(sketch, "E188.MirrorCS", {"start": v(-3.93, 0.78) * mm, "end": v(-3.88, 5.84) * mm});
            skLineSegment(sketch, "E189.MirrorCS", {"start": v(-6.72, 30.38) * mm, "end": v(-7.2, 24.76) * mm});
            skArc(sketch, "E190.MirrorCS", {"start": v(-3.58, 18.88) * mm, "mid": v(-4.38, 23.51) * mm, "end": v(-3.05, 28.02) * mm});
            skLineSegment(sketch, "E191.MirrorCS", {"start": v(-17, -6.23) * mm, "end": v(-18.2, -4.79) * mm});
            skFitSpline(sketch, "E192.MirrorCS", {"points": [v(-18.61, 0.8) * mm, v(-20.64, 0.96) * mm, v(-23.76, 2.29) * mm, v(-23, 1.14) * mm, v(-20.64, -0.64) * mm, v(-18.61, -0.99) * mm], "startDerivative": vector(-9, -1.2) * mm, "endDerivative": vector(10.69, -0.53) * mm});
            skArc(sketch, "E193.MirrorCS", {"start": v(-6, 25.8) * mm, "mid": v(-4.95, 27.5) * mm, "end": v(-3.05, 28.02) * mm});
            skLineSegment(sketch, "E194.MirrorCS", {"start": v(-2.42, -9.56) * mm, "end": v(-2.52, -0.32) * mm});
            skLineSegment(sketch, "E195.MirrorCS", {"start": v(-1.43, -10.06) * mm, "end": v(-1.43, 2.37) * mm});
            skFitSpline(sketch, "E196.MirrorCS", {"points": [v(-8.47, -19.62) * mm, v(-5.7, -22.53) * mm, v(-5.7, -25.34) * mm, v(-1.6, -26.85) * mm, v(-0.8, -26.85) * mm], "startDerivative": vector(12.98, -8.92) * mm, "endDerivative": vector(4.07, 0.48) * mm});
            skFitSpline(sketch, "E197.MirrorCS", {"points": [v(-4.03, -26.34) * mm, v(-4.03, -23.16) * mm, v(-5.06, -19.2) * mm, v(-5.7, -17.43) * mm, v(-5.06, -15.96) * mm, v(-4.03, -16.14) * mm, v(-3.05, -18.55) * mm, v(-2.42, -22.53) * mm, v(-1.9, -25.48) * mm, v(-0.8, -25.93) * mm], "startDerivative": vector(1.6, 23.43) * mm, "endDerivative": vector(16.16, -2.15) * mm});
            skFitSpline(sketch, "E198.MirrorCS", {"points": [v(-7.36, -26.46) * mm, v(-7.56, -28.68) * mm, v(-8.3, -31.39) * mm, v(-6.7, -30.43) * mm, v(-5.06, -29.98) * mm, v(-4.37, -31.12) * mm, v(-4.6, -32.48) * mm, v(-4.59, -33.58) * mm, v(-4.1, -33.56) * mm, v(-3.72, -32.47) * mm, v(-2.7, -31.57) * mm, v(-1.9, -31.46) * mm, v(-1.6, -32.29) * mm, v(-0.8, -32.72) * mm], "startDerivative": vector(1, -19.1) * mm, "endDerivative": vector(15.31, -4.03) * mm});
            skLineSegment(sketch, "E199.MirrorCS", {"start": v(-1.33, 22.92) * mm, "end": v(-0.8, 31.03) * mm});
            skFitSpline(sketch, "E200.MirrorCS", {"points": [v(-7.36, -26.46) * mm, v(-7.36, -22.53) * mm, v(-8.47, -19.62) * mm, v(-7.36, -14.52) * mm, v(-5.75, -10.91) * mm, v(-5.06, -6.36) * mm, v(-5.7, -0.98) * mm, v(-9.5, 1.72) * mm], "startDerivative": vector(3.54, 31.13) * mm, "endDerivative": vector(-30.9, 14.24) * mm});
            skLineSegment(sketch, "E201.MirrorCS", {"start": v(-4.13, 41.02) * mm, "end": v(-4.13, 27.92) * mm});
            skLineSegment(sketch, "E202.MirrorCS", {"start": v(-1.33, 22.92) * mm, "end": v(-4.13, 41.02) * mm});
            skFitSpline(sketch, "E203.MirrorCS", {"points": [v(-18.61, 9.47) * mm, v(-22.28, 9.47) * mm, v(-25.19, 14.9) * mm, v(-26.45, 22.96) * mm, v(-28.98, 25.4) * mm], "startDerivative": vector(-18.53, -4.1) * mm, "endDerivative": vector(-14.4, 8.9) * mm});
            skFitSpline(sketch, "E204.MirrorCS", {"points": [v(-20.64, 55.21) * mm, v(-18.74, 51.8) * mm, v(-18.36, 45.6) * mm, v(-23.3, 34.22) * mm, v(-24.18, 28.02) * mm, v(-21.65, 18.47) * mm, v(-18.74, 13.26) * mm, v(-18.61, 9.47) * mm], "startDerivative": vector(19, -28.92) * mm, "endDerivative": vector(-3.8, -35.47) * mm});
            skFitSpline(sketch, "E205.MirrorCS", {"points": [v(-11.02, 5.04) * mm, v(-14.76, 9.8) * mm, v(-18.74, 18.47) * mm, v(-21.65, 26) * mm, v(-21.65, 34.22) * mm, v(-18.74, 40.66) * mm, v(-17.18, 46.3) * mm, v(-17.54, 50.59) * mm, v(-20.64, 55.21) * mm], "startDerivative": vector(-32.67, 35.42) * mm, "endDerivative": vector(-33.02, 40.5) * mm});
            skFitSpline(sketch, "E206.MirrorCS", {"points": [v(-28.98, 25.4) * mm, v(-28, 22.96) * mm, v(-28, 13.26) * mm, v(-24.68, 6.94) * mm, v(-18.61, 2.39) * mm], "startDerivative": vector(7.89, -11.91) * mm, "endDerivative": vector(24.05, -15.72) * mm});
            skFitSpline(sketch, "E207.MirrorCS", {"points": [v(-17, -6.23) * mm, v(-17, -7.8) * mm, v(-19.6, -12.4) * mm, v(-22.3, -16.75) * mm, v(-26.45, -18.78) * mm, v(-27.68, -19.3) * mm, v(-24.9, -19.58) * mm, v(-21.52, -18.1) * mm, v(-18.61, -13.7) * mm, v(-13.26, -13.67) * mm, v(-11.7, -15.63) * mm, v(-12.76, -17.65) * mm, v(-15.8, -17.65) * mm, v(-15.04, -18.66) * mm, v(-13.2, -19.64) * mm, v(-10.67, -19.58) * mm, v(-9.51, -22.53) * mm, v(-12.9, -27.54) * mm, v(-10.85, -27.54) * mm, v(-7.36, -26.46) * mm], "startDerivative": vector(7.73, -38) * mm, "endDerivative": vector(58.93, 20.62) * mm});
            skFitSpline(sketch, "E208.MirrorCS", {"points": [v(-9.9, 17.62) * mm, v(-12.36, 20.35) * mm, v(-17, 28.02) * mm, v(-16.3, 37.16) * mm, v(-15.83, 45.86) * mm, v(-16.84, 51.42) * mm, v(-20.64, 55.21) * mm], "startDerivative": vector(-17.57, 18.84) * mm, "endDerivative": vector(-30.07, 23.23) * mm});
            skLineSegment(sketch, "E209", {"start": v(1.57, 17.44) * mm, "end": v(2, 18.88) * mm});
            skLineSegment(sketch, "E210", {"start": v(-3.15, 17.44) * mm, "end": v(-3.58, 18.88) * mm});
            skArc(sketch, "E211", {"start": v(0.61, 16.38) * mm, "mid": v(-0.8, 16.56) * mm, "end": v(-2.2, 16.38) * mm});
            skArc(sketch, "E212", {"start": v(-5.19, 6.23) * mm, "mid": v(-0.8, 4.54) * mm, "end": v(3.6, 6.23) * mm});
            skLineSegment(sketch, "E213", {"start": v(-1.43, -10.06) * mm, "end": v(-0.16, -10.06) * mm});
            skArc(sketch, "E214", {"start": v(-0.8, 3.35) * mm, "mid": v(-1.4, 4.65) * mm, "end": v(-2.7, 5.28) * mm});
            skPoint(sketch, "E214.startSnap0", {"position": v(-0.8, 4.54) * mm});
            skArc(sketch, "E215.MirrorCS", {"start": v(-0.8, 3.35) * mm, "mid": v(-0.17, 4.65) * mm, "end": v(1.12, 5.28) * mm});
            skSolve(sketch);
        }
        {
            var Q0;
            Q0=makeQuery(id+"F6.imprint","IMPRINT",FACE,{"disambiguationData":[TD([[makeQuery(id+"F6.imprint","IMPRINT",EDGE,{"derivedFrom":sQuery(id+"F6.wireOp",EDGE,"E165.MirrorCS")}),1.0]])]});
            var Q1;
            Q1=makeQuery(id+"F6.imprint","IMPRINT",FACE,{"disambiguationData":[TD([[makeQuery(id+"F6.imprint","IMPRINT",EDGE,{"derivedFrom":sQuery(id+"F6.wireOp",EDGE,"E88")}),-1.0]])]});
            var Q2;
            {var subQ0=sQuery(id+"F6.wireOp",EDGE,"E178.MirrorC");var subQ1=sQuery(id+"F6.wireOp",EDGE,"E177.MirrorC");var subQ2=makeQuery(id+"F6.imprint","INTERSECT",VERTEX,{"disambiguationData":[OD(0.0)],"derivedFrom":[subQ1,subQ0]});Q2=makeQuery(id+"F6.imprint","IMPRINT",FACE,{"disambiguationData":[TD([[makeQuery(id+"F6.imprint","IMPRINT",EDGE,{"disambiguationData":[TD([[subQ2,1.0]])],"derivedFrom":subQ1}),1.0]])]});}
            var Q3;
            {var subQ0=sQuery(id+"F6.wireOp",EDGE,"E101");var subQ1=sQuery(id+"F6.wireOp",EDGE,"E100");var subQ2=makeQuery(id+"F6.imprint","INTERSECT",VERTEX,{"disambiguationData":[OD(0.0)],"derivedFrom":[subQ1,subQ0]});Q3=makeQuery(id+"F6.imprint","IMPRINT",FACE,{"disambiguationData":[TD([[makeQuery(id+"F6.imprint","IMPRINT",EDGE,{"disambiguationData":[TD([[subQ2,1.0]])],"derivedFrom":subQ1}),-1.0]])]});}
            var Q4;
            {var subQ4=sQuery(id+"F6.wireOp",EDGE,"E95");Q4=makeQuery(id+"F6.imprint","IMPRINT",FACE,{"disambiguationData":[TD([[makeQuery(id+"F6.imprint","IMPRINT",EDGE,{"derivedFrom":subQ4}),-1.0]])]});}
            var Q5;
            {var subQ3=sQuery(id+"F6.wireOp",EDGE,"E99");Q5=makeQuery(id+"F6.imprint","IMPRINT",FACE,{"disambiguationData":[TD([[makeQuery(id+"F6.imprint","IMPRINT",EDGE,{"derivedFrom":subQ3}),1.0]])]});}
            extrude(context, id + "F7", {"entities" : qUnion([Q0, Q1, Q2, Q3, Q4, Q5]), "oppositeDirection" : true, "depth" : .2 * mm, "offsetDistance" : 25.4 * mm});
        }
        {
            var Q0;
            Q0=makeQuery(id+"F6.imprint","IMPRINT",FACE,{"disambiguationData":[TD([[makeQuery(id+"F6.imprint","IMPRINT",EDGE,{"derivedFrom":sQuery(id+"F6.wireOp",EDGE,"E47")}),-1.0]])]});
            var Q1;
            {var subQ1=sQuery(id+"F6.wireOp",EDGE,"E186.MirrorCS");var subQ5=sQuery(id+"F6.wireOp",EDGE,"E212");var subQ6=makeQuery(id+"F6.imprint","INTERSECT",VERTEX,{"derivedFrom":[subQ1,subQ5]});Q1=makeQuery(id+"F6.imprint","IMPRINT",FACE,{"disambiguationData":[TD([[makeQuery(id+"F6.imprint","IMPRINT",EDGE,{"disambiguationData":[TD([[subQ6,-1.0]])],"derivedFrom":subQ5}),1.0]])]});}
            var Q2;
            {var subQ2=sQuery(id+"F6.wireOp",EDGE,"E52");var subQ4=sQuery(id+"F6.wireOp",EDGE,"E212");var subQ5=makeQuery(id+"F6.imprint","INTERSECT",VERTEX,{"derivedFrom":[subQ2,subQ4]});Q2=makeQuery(id+"F6.imprint","IMPRINT",FACE,{"disambiguationData":[TD([[makeQuery(id+"F6.imprint","IMPRINT",EDGE,{"disambiguationData":[TD([[subQ5,1.0]])],"derivedFrom":subQ4}),1.0]])]});}
            var Q3;
            Q3=makeQuery(id+"F6.imprint","IMPRINT",FACE,{"disambiguationData":[TD([[makeQuery(id+"F6.imprint","IMPRINT",EDGE,{"derivedFrom":sQuery(id+"F6.wireOp",EDGE,"E50")}),1.0]])]});
            var Q4;
            Q4=makeQuery(id+"F6.imprint","IMPRINT",FACE,{"disambiguationData":[TD([[makeQuery(id+"F6.imprint","IMPRINT",EDGE,{"derivedFrom":sQuery(id+"F6.wireOp",EDGE,"E107")}),1.0]])]});
            var Q5;
            {var subQ3=sQuery(id+"F6.wireOp",EDGE,"E175.MirrorCS");Q5=makeQuery(id+"F6.imprint","IMPRINT",FACE,{"disambiguationData":[TD([[makeQuery(id+"F6.imprint","IMPRINT",EDGE,{"derivedFrom":subQ3}),1.0]])]});}
            var Q6;
            {var subQ3=sQuery(id+"F6.wireOp",EDGE,"E68");Q6=makeQuery(id+"F6.imprint","IMPRINT",FACE,{"disambiguationData":[TD([[makeQuery(id+"F6.imprint","IMPRINT",EDGE,{"derivedFrom":subQ3}),1.0]])]});}
            var Q7;
            {var subQ1=sQuery(id+"F6.wireOp",EDGE,"E59");Q7=makeQuery(id+"F6.imprint","IMPRINT",FACE,{"disambiguationData":[TD([[makeQuery(id+"F6.imprint","IMPRINT",EDGE,{"derivedFrom":subQ1}),1.0]])]});}
            extrude(context, id + "F8", {"entities" : qUnion([Q0, Q1, Q2, Q3, Q4, Q5, Q6, Q7]), "operationType" : NewBodyOperationType.ADD, "oppositeDirection" : true, "depth" : .3 * mm, "offsetDistance" : 25.4 * mm});
        }
        {
            var Q0;
            {var subQ4=sQuery(id+"F6.wireOp",EDGE,"E68");Q0=makeQuery(id+"F6.imprint","IMPRINT",FACE,{"disambiguationData":[TD([[makeQuery(id+"F6.imprint","IMPRINT",EDGE,{"derivedFrom":subQ4}),-1.0]])]});}
            var Q1;
            {var subQ11=sQuery(id+"F6.wireOp",EDGE,"E175.MirrorCS");Q1=makeQuery(id+"F6.imprint","IMPRINT",FACE,{"disambiguationData":[TD([[makeQuery(id+"F6.imprint","IMPRINT",EDGE,{"derivedFrom":subQ11}),-1.0]])]});}
            var Q2;
            Q2=makeQuery(id+"F6.imprint","IMPRINT",FACE,{"disambiguationData":[TD([[makeQuery(id+"F6.imprint","IMPRINT",EDGE,{"derivedFrom":sQuery(id+"F6.wireOp",EDGE,"E55")}),1.0]])]});
            var Q3;
            {var subQ4=sQuery(id+"F6.wireOp",EDGE,"E148.MirrorCS");Q3=makeQuery(id+"F6.imprint","IMPRINT",FACE,{"disambiguationData":[TD([[makeQuery(id+"F6.imprint","IMPRINT",EDGE,{"derivedFrom":subQ4}),1.0]])]});}
            var Q4;
            Q4=makeQuery(id+"F6.imprint","IMPRINT",FACE,{"disambiguationData":[TD([[makeQuery(id+"F6.imprint","IMPRINT",EDGE,{"derivedFrom":sQuery(id+"F6.wireOp",EDGE,"E107")}),-1.0]])]});
            var Q5;
            {var subQ1=sQuery(id+"F6.wireOp",EDGE,"E157.MirrorCS");var subQ3=sQuery(id+"F6.wireOp",EDGE,"E188.MirrorCS");var subQ4=makeQuery(id+"F6.imprint","INTERSECT",VERTEX,{"derivedFrom":[subQ1,subQ3]});Q5=makeQuery(id+"F6.imprint","IMPRINT",FACE,{"disambiguationData":[TD([[makeQuery(id+"F6.imprint","IMPRINT",EDGE,{"disambiguationData":[TD([[subQ4,1.0]])],"derivedFrom":subQ3}),-1.0]])]});}
            var Q6;
            {var subQ5=sQuery(id+"F6.wireOp",EDGE,"E157.MirrorCS");var subQ7=sQuery(id+"F6.wireOp",EDGE,"E53");var subQ8=makeQuery(id+"F6.imprint","INTERSECT",VERTEX,{"disambiguationData":[OD(0.0)],"derivedFrom":[subQ7,subQ5]});Q6=makeQuery(id+"F6.imprint","IMPRINT",FACE,{"disambiguationData":[TD([[makeQuery(id+"F6.imprint","IMPRINT",EDGE,{"disambiguationData":[TD([[subQ8,-1.0]])],"derivedFrom":subQ7}),-1.0]])]});}
            var Q7;
            {var subQ0=sQuery(id+"F6.wireOp",EDGE,"E214");var subQ1=sQuery(id+"F6.wireOp",EDGE,"E212");var subQ2=makeQuery(id+"F6.imprint","INTERSECT",VERTEX,{"derivedFrom":[subQ1,subQ0]});Q7=makeQuery(id+"F6.imprint","IMPRINT",FACE,{"disambiguationData":[TD([[makeQuery(id+"F6.imprint","IMPRINT",EDGE,{"disambiguationData":[TD([[subQ2,-1.0]])],"derivedFrom":subQ1}),-1.0]])]});}
            var Q8;
            {var subQ0=sQuery(id+"F6.wireOp",EDGE,"E53");var subQ5=sQuery(id+"F6.wireOp",EDGE,"E54");var subQ6=makeQuery(id+"F6.imprint","INTERSECT",VERTEX,{"derivedFrom":[subQ0,subQ5]});Q8=makeQuery(id+"F6.imprint","IMPRINT",FACE,{"disambiguationData":[TD([[makeQuery(id+"F6.imprint","IMPRINT",EDGE,{"disambiguationData":[TD([[subQ6,1.0]])],"derivedFrom":subQ5}),1.0]])]});}
            var Q9;
            Q9=makeQuery(id+"F6.imprint","IMPRINT",FACE,{"disambiguationData":[TD([[makeQuery(id+"F6.imprint","IMPRINT",EDGE,{"derivedFrom":sQuery(id+"F6.wireOp",EDGE,"E47")}),1.0]])]});
            var Q10;
            Q10=makeQuery(id+"F6.imprint","IMPRINT",FACE,{"disambiguationData":[TD([[makeQuery(id+"F6.imprint","IMPRINT",EDGE,{"derivedFrom":sQuery(id+"F6.wireOp",EDGE,"E182.MirrorCS")}),-1.0]])]});
            var Q11;
            Q11=makeQuery(id+"F6.imprint","IMPRINT",FACE,{"disambiguationData":[TD([[makeQuery(id+"F6.imprint","IMPRINT",EDGE,{"derivedFrom":sQuery(id+"F6.wireOp",EDGE,"E168.MirrorCS")}),1.0]])]});
            var Q12;
            Q12=makeQuery(id+"F6.imprint","IMPRINT",FACE,{"disambiguationData":[TD([[makeQuery(id+"F6.imprint","IMPRINT",EDGE,{"derivedFrom":sQuery(id+"F6.wireOp",EDGE,"E71")}),-1.0]])]});
            var Q13;
            Q13=makeQuery(id+"F6.imprint","IMPRINT",FACE,{"disambiguationData":[TD([[makeQuery(id+"F6.imprint","IMPRINT",EDGE,{"derivedFrom":sQuery(id+"F6.wireOp",EDGE,"E76")}),1.0]])]});
            extrude(context, id + "F9", {"entities" : qUnion([Q0, Q1, Q2, Q3, Q4, Q5, Q6, Q7, Q8, Q9, Q10, Q11, Q12, Q13]), "oppositeDirection" : true, "depth" : .4 * mm, "offsetDistance" : 25.4 * mm});
        }
    });
